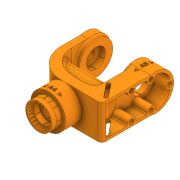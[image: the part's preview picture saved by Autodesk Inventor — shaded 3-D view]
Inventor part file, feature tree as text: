
AUTODESK INVENTOR PART (.ipt)
format: ipt  version: 2020 (Build 240168000, 168)  size: 2,074,624 bytes
history: native  units: in
note: dims shown in document units (in); Inventor stores cm internally (conversion verified against a paired STEP export)
features: sketch x41, extrude x37, projected_geometry x29, fillet x7, chamfer x6, plane x6, emboss x3
ambient origin geometry x8: Origin, YZ Plane, XZ Plane, XY Plane, X Axis, Y Axis, Z Axis, Center Point
bodies: Solid1 (feature_tree)
feature tree (129):
  extrude  "Extrusion1"  Depth=2.0472in
  extrude  "Extrusion2"  Depth=1.1063in
  chamfer  "Chamfer2"  Distance=0.2756in
  extrude  "Extrusion4"  Depth=0.0157in
  extrude  "Extrusion7"  Depth=0.2756in TaperAngle=0.0deg
  chamfer  "Chamfer4"  Distance=0.0394in
  extrude  "Extrusion8"  Depth=0.315in
  sketch  "Sketch12"  dims[d39=1.4567in d57=0.0394in d58=0.0in]
  plane  "Work Plane1"
  sketch  "Sketch13"  dims[d59=0.315in d60=0.125in d61=0.0137in d67=0.0157in]
  extrude  "Extrusion10"  Depth=0.0394in TaperAngle=0.0deg
  extrude  "Extrusion11"  Depth=0.0866in
  chamfer  "Chamfer5"  Distance=9.4488in Angle=360.0deg
  extrude  "Extrusion12"  Depth=0.2756in TaperAngle=0.0deg
  plane  "Work Plane2"
  extrude  "Extrusion13"  Depth=0.315in
  plane  "Work Plane3"
  extrude  "Extrusion14"  Depth=1.0236in
  extrude  "Extrusion15"  Depth=0.8858in
  extrude  "Extrusion16"  Depth=0.3937in
  extrude  "Extrusion17"  Depth=1.378in
  sketch  "Sketch21"  dims[d107=0.315in d108=0.0in d109=0.315in d110=0.125in d111=0.0137in]
  extrude  "Extrusion19"  Depth=0.5906in
  sketch  "Sketch23"  dims[d112=1.0in d113=0.0in d114=1.0236in]
  extrude  "Extrusion20"  Depth=0.1575in TaperAngle=0.0deg
  extrude  "Extrusion21"  Depth=0.1575in TaperAngle=0.0deg
  extrude  "Extrusion22"  Depth=4.2323in
  extrude  "Extrusion23"  Depth=0.1575in
  extrude  "Extrusion24"  Depth=1.1024in
  extrude  "Extrusion25"  Depth=0.4921in
  extrude  "Extrusion26"  Depth=0.75in
  extrude  "Extrusion27"  Depth=0.2165in TaperAngle=0.0deg
  extrude  "Extrusion28"  Depth=0.1575in
  extrude  "Extrusion29"  Depth=1.1811in
  plane  "Work Plane4"
  extrude  "Extrusion30"  Depth=0.315in TaperAngle=0.0deg
  fillet  "Fillet1"  Radius=0.3937in
  fillet  "Fillet2"  Radius=0.315in
  extrude  "Extrusion31"  Depth=0.315in TaperAngle=0.0deg
  extrude  "Extrusion32"  Depth=0.315in TaperAngle=0.0deg
  extrude  "Extrusion33"  Depth=0.3937in TaperAngle=0.0deg
  fillet  "Fillet3"  Radius=0.2165in
  extrude  "Extrusion34"  Depth=0.4724in
  chamfer  "Chamfer6"  Distance=0.2756in
  chamfer  "Chamfer7"  Distance=0.0394in
  extrude  "Extrusion35"  Depth=0.0394in
  extrude  "Extrusion36"  Depth=1.0in TaperAngle=0.0deg
  fillet  "Fillet5"  Radius=0.1575in
  extrude  "Extrusion38"  Depth=0.315in
  extrude  "Extrusion39"  Depth=0.2264in
  extrude  "Extrusion40"  Depth=0.2264in TaperAngle=360.0deg
  fillet  "Fillet7"  Radius=1.0in
  extrude  "Extrusion41"  Depth=0.2264in TaperAngle=0.0deg
  chamfer  "Chamfer8"  Distance=0.1969in
  extrude  "Extrusion42"  Depth=0.3937in TaperAngle=0.0deg
  plane  "Work Plane6"
  emboss  "Emboss1"
  emboss  "Emboss2"
  plane  "Work Plane7"
  emboss  "Emboss3"
  extrude  "Extrusion43"  Depth=0.2264in
  fillet  "Fillet9"  Radius=0.0787in
  fillet  "Fillet10"  Radius=0.1969in
  sketch  "Sketch1"  dims[d0=0.6299in d1=2.0472in]
  sketch  "Sketch2"  dims[d2=0.9449in d3=0.0in d4=1.1063in]
  sketch  "Sketch4"  dims[d5=1.5748in d6=0.2756in d7=0.0in]
  sketch  "Sketch8"  dims[d11=0.2756in d12=0.125in d13=0.0137in d25=0.0157in]
  projected_geometry  "Projected Loop2"
  sketch  "Sketch10"  dims[d26=6.2992in d28=360.0deg d30=0.2756in d31=0.0in]
  sketch  "Sketch14"  dims[d68=4.7244in d70=360.0deg d72=0.0394in d73=0.0in]
  sketch  "Sketch15"  dims[d83=0.0591in d84=0.0866in]
  projected_geometry  "Projected Loop4"
  sketch  "Sketch16"  dims[d85=0.0827in]
  sketch  "Sketch17"  dims[d86=0.0827in]
  projected_geometry  "Projected Loop5"
  sketch  "Sketch18"  dims[d87=0.0827in d88=9.4488in d90=360.0deg]
  projected_geometry  "Projected Loop6"
  projected_geometry  "Projected Loop7"
  sketch  "Sketch19"  dims[d92=0.2756in]
  projected_geometry  "Projected Loop8"
  projected_geometry  "Projected Loop9"
  sketch  "Sketch20"  dims[d94=9.4488in d95=0.0827in d96=0.0827in d97=0.0827in d98=360.0deg d105=0.2756in d106=0.0in]
  projected_geometry  "Projected Loop10"
  projected_geometry  "Projected Loop11"
  projected_geometry  "Projected Loop12"
  projected_geometry  "Projected Loop13"
  sketch  "Sketch25"  dims[d115=0.7874in d117=0.8858in]
  sketch  "Sketch26"  dims[d118=2.7559in d119=0.3937in]
  projected_geometry  "Projected Loop16"
  projected_geometry  "Projected Loop17"
  sketch  "Sketch27"  dims[d120=0.5906in d121=1.378in]
  projected_geometry  "Projected Loop18"
  projected_geometry  "Projected Loop19"
  sketch  "Sketch28"  dims[d123=3.4941in d124=0.5906in]
  projected_geometry  "Projected Loop20"
  projected_geometry  "Projected Loop21"
  sketch  "Sketch29"  dims[d126=1.9685in d129=0.1575in d130=0.0in]
  projected_geometry  "Projected Loop22"
  projected_geometry  "Projected Loop23"
  sketch  "Sketch30"  dims[d131=-2.0472in d132=0.1575in d133=0.0in]
  projected_geometry  "Projected Loop24"
  sketch  "Sketch31"  dims[d134=2.126in d136=4.2323in]
  sketch  "Sketch32"  dims[d137=0.1575in d138=0.1575in]
  sketch  "Sketch34"  dims[d139=0.4921in d140=0.0in d141=1.1024in]
  projected_geometry  "Projected Loop25"
  sketch  "Sketch35"  dims[d142=1.1614in d143=0.4921in]
  sketch  "Sketch36"  dims[d144=0.3445in d145=0.75in]
  projected_geometry  "Projected Loop26"
  sketch  "Sketch37"  dims[d146=0.1575in d147=0.0in d148=0.2165in d149=0.0in]
  projected_geometry  "Projected Loop27"
  sketch  "Sketch38"  dims[d152=1.0039in d153=0.0in d154=0.1575in]
  projected_geometry  "Projected Loop28"
  sketch  "Sketch39"  dims[d155=0.1575in d160=1.1811in]
  projected_geometry  "Projected Loop29"
  sketch  "Sketch40"  dims[d161=0.1969in d162=0.0in d163=0.315in d164=0.0in d165=0.3937in d166=0.0in d167=0.315in d168=0.0in]
  sketch  "Sketch41"  dims[d169=0.315in d170=0.0in d171=0.315in d172=0.0in]
  projected_geometry  "Projected Loop30"
  sketch  "Sketch43"  dims[d173=0.315in d174=0.0in d175=0.315in d176=0.0in]
  projected_geometry  "Projected Loop31"
  sketch  "Sketch44"  dims[d177=1.1024in d178=0.3937in d179=0.0in d180=0.2165in d181=0.0in]
  sketch  "Sketch45"  dims[d183=-0.0197in d184=0.4724in d185=0.2756in d186=0.0in]
  sketch  "Sketch46"  dims[d187=0.5512in]
  projected_geometry  "Projected Loop32"
  sketch  "Sketch47"  dims[d188=0.2165in d189=0.0394in d190=0.0in]
  projected_geometry  "Projected Loop33"
  sketch  "Sketch48"  dims[d191=0.0394in d192=0.0in d193=0.001in]
  sketch  "Sketch49"  dims[d194=0.001in d195=1.0in d196=0.0in d197=0.1575in]
  sketch  "Sketch50"  dims[d198=1.0in d199=0.0in d200=0.315in d201=0.125in d202=0.0137in]
  sketch  "Sketch52"  dims[d203=0.315in d204=0.125in d205=0.0137in d206=0.0157in d207=2.3622in d209=360.0deg d211=1.0in d212=0.0in d213=1.0in d214=0.0in d221=0.1969in d222=0.3937in d223=0.0in d224=0.1575in d225=0.0787in d226=0.1969in d227=0.0in d229=0.1181in d230=1.0039in d231=0.4134in d232=0.5118in d233=0.0984in d235=0.0197in d236=0.1181in d237=0.1181in d238=0.2047in d239=0.2047in d240=0.0in d241=0.0in d242=0.2362in d243=0.0787in d244=0.0787in d251=0.0787in d252=0.0787in d253=0.2756in d254=0.4724in d255=0.2756in d256=0.4724in d257=0.2756in d258=0.4724in d259=0.2756in d260=0.4724in d261=0.1575in d262=0.0in d263=0.0787in d264=0.125in d265=45.0deg d266=1.0in d267=0.0in d269=0.0394in d270=0.0in d271=0.0394in d272=0.0in d273=0.0394in d274=0.0in d275=0.0039in d276=0.0787in d277=1.0in d278=0.0in d279=0.122in d280=0.2264in d282=0.1378in d283=0.2047in]
